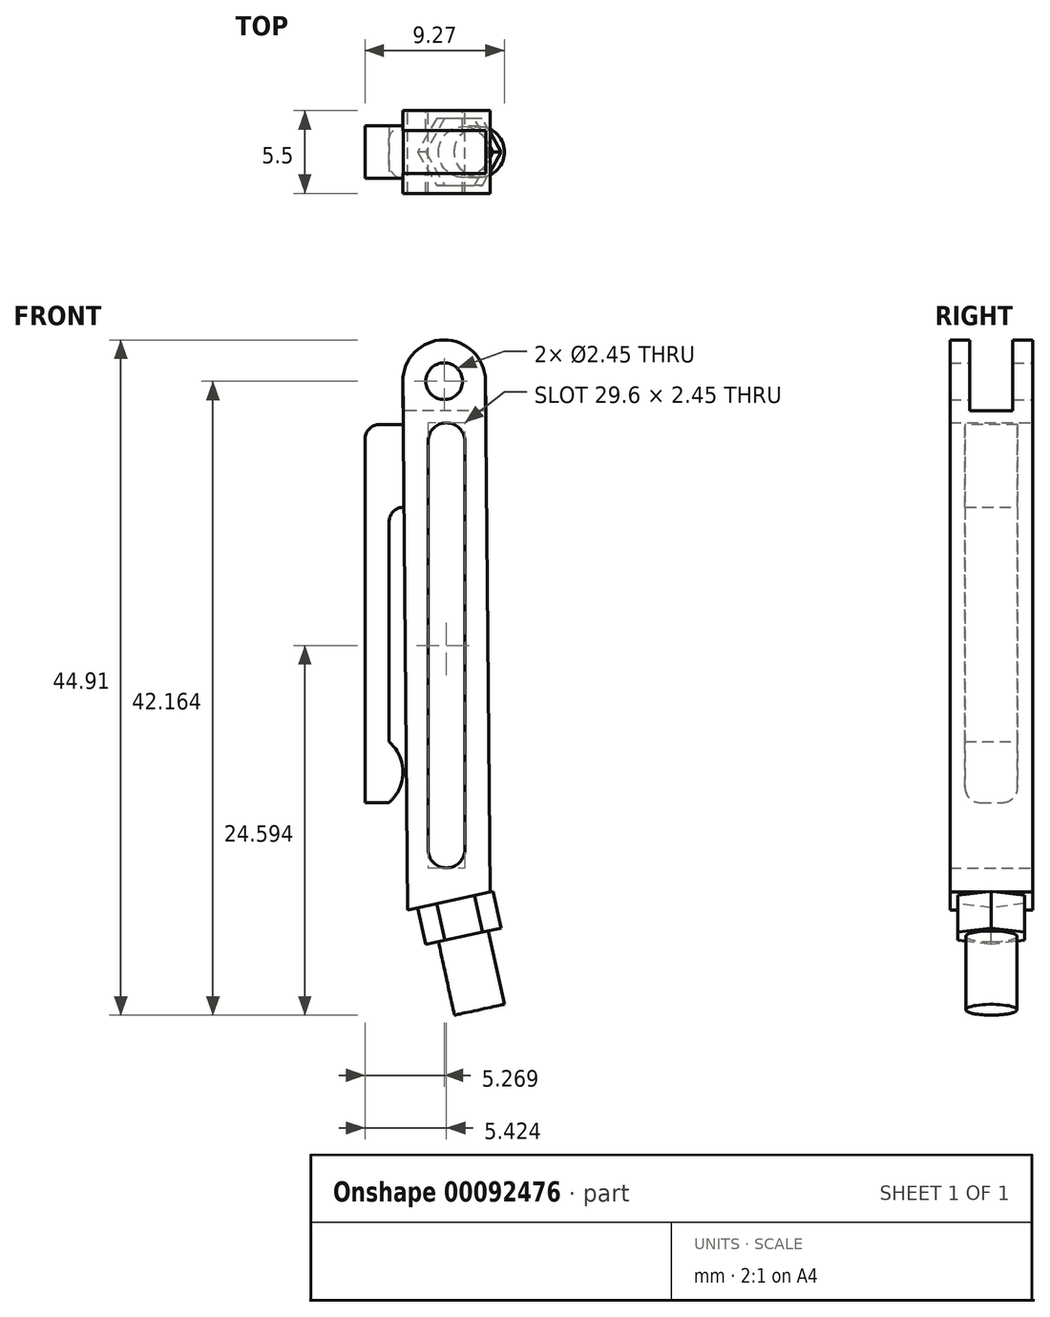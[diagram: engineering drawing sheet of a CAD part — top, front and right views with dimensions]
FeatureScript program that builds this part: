
annotation { "Feature Type Name" : "Feature", "Feature Type Description" : "" }
export const myFeature = defineFeature(function(context is Context, id is Id, definition is map)
    precondition{}
    {
        {
            var Q0;
            Q0=qCreatedBy(makeId("Front.planeOp"),FACE);
            var sketch = newSketch(context, id + "F0", { "sketchPlane" : qUnion([Q0])});
            skLineSegment(sketch, "E0.left", {"start": v(2.74, 2.18) * mm, "end": v(2.44, 36.18) * mm});
            skLineSegment(sketch, "E0.right", {"start": v(-2.75, 0.99) * mm, "end": v(-3.06, 36.13) * mm});
            skPoint(sketch, "E0.middle", {"position": v(-0.16, 18.58) * mm});
            skArc(sketch, "E1", {"start": v(2.44, 36.18) * mm, "mid": v(-0.34, 38.9) * mm, "end": v(-3.06, 36.13) * mm});
            skCircle(sketch, "E2", {"center": v(-0.31, 36.15) * mm, "radius": 1.23 * mm});
            skLineSegment(sketch, "E3.left", {"start": v(-1.38, 32.16) * mm, "end": v(-1.38, 5) * mm});
            skLineSegment(sketch, "E3.right", {"start": v(1.07, 32.16) * mm, "end": v(1.07, 5) * mm});
            skArc(sketch, "E4", {"start": v(1.07, 32.16) * mm, "mid": v(-0.16, 33.38) * mm, "end": v(-1.38, 32.16) * mm});
            skArc(sketch, "E5", {"start": v(-1.38, 5) * mm, "mid": v(-0.16, 3.78) * mm, "end": v(1.07, 5) * mm});
            skLineSegment(sketch, "E6", {"start": v(-2.75, 0.99) * mm, "end": v(2.74, 2.18) * mm});
            skSolve(sketch);
        }
        {
            var Q0;
            Q0=qSketchRegion(id+"F0",true);
            extrude(context, id + "F1", {"entities" : qUnion([Q0]), "depth" : 5.5 * mm, "symmetric" : true});
        }
        {
            var Q0;
            Q0=qCreatedBy(makeId("Front.planeOp"),FACE);
            var sketch = newSketch(context, id + "F2", { "sketchPlane" : qUnion([Q0])});
            skLineSegment(sketch, "E7", {"start": v(-2.9, 33.29) * mm, "end": v(-5.58, 33.29) * mm});
            skLineSegment(sketch, "E8", {"start": v(-5.58, 33.29) * mm, "end": v(-5.58, 8.14) * mm});
            skLineSegment(sketch, "E9", {"start": v(-5.58, 8.14) * mm, "end": v(-3.98, 8.14) * mm});
            skLineSegment(sketch, "E10", {"start": v(-3.98, 8.14) * mm, "end": v(-3.98, 27.78) * mm});
            skLineSegment(sketch, "E11", {"start": v(-3.98, 27.78) * mm, "end": v(-2.9, 27.78) * mm});
            skLineSegment(sketch, "E12", {"start": v(-2.9, 27.78) * mm, "end": v(-2.9, 33.29) * mm});
            skArc(sketch, "E13", {"start": v(-3.98, 8.14) * mm, "mid": v(-3.05, 10.16) * mm, "end": v(-3.98, 12.19) * mm});
            skSolve(sketch);
        }
        {
            var Q0;
            Q0=makeQuery(id+"F2.imprint","IMPRINT",FACE,{"disambiguationData":[TD([[makeQuery(id+"F2.imprint","IMPRINT",EDGE,{"derivedFrom":sQuery(id+"F2.wireOp",EDGE,"E7")}),1.0]])]});
            var Q1;
            {var subQ0=sQuery(id+"F2.wireOp",EDGE,"E13");Q1=makeQuery(id+"F2.imprint","IMPRINT",FACE,{"disambiguationData":[TD([[makeQuery(id+"F2.imprint","IMPRINT",EDGE,{"derivedFrom":subQ0}),1.0]])]});}
            extrude(context, id + "F3", {"entities" : qUnion([Q0, Q1]), "operationType" : NewBodyOperationType.ADD, "depth" : 3.5 * mm, "symmetric" : true});
        }
        {
            var Q0;
            Q0=qCreatedBy(makeId("Right.planeOp"),FACE);
            var sketch = newSketch(context, id + "F4", { "sketchPlane" : qUnion([Q0])});
            skLineSegment(sketch, "E14.bottom", {"start": v(1.44, 34.2) * mm, "end": v(-1.44, 34.2) * mm});
            skLineSegment(sketch, "E14.top", {"start": v(1.44, 40.18) * mm, "end": v(-1.44, 40.18) * mm});
            skLineSegment(sketch, "E14.left", {"start": v(1.44, 34.2) * mm, "end": v(1.44, 40.18) * mm});
            skLineSegment(sketch, "E14.right", {"start": v(-1.44, 34.2) * mm, "end": v(-1.44, 40.18) * mm});
            skPoint(sketch, "E14.middle", {"position": v(0, 37.2) * mm});
            skSolve(sketch);
        }
        {
            var Q0;
            Q0=qSketchRegion(id+"F4",true);
            extrude(context, id + "F5", {"entities" : qUnion([Q0]), "operationType" : NewBodyOperationType.REMOVE, "depth" : 26 * mm, "symmetric" : true});
        }
        {
            var Q0;
            Q0=makeQuery(id+"F3.opExtrude","SWEPT_EDGE",EDGE,{"disambiguationData":[OSD([sQuery(id+"F2.wireOp",EDGE,"E10"),sQuery(id+"F2.wireOp",EDGE,"E11")])]});
            fillet(context, id + "F6", {"entities" : qUnion([Q0]), "radius" : 1 * mm, "tangentPropagation" : true, "allowEdgeOverflow" : false});
        }
        {
            var Q0;
            Q0=makeQuery(id+"F3.opExtrude","SWEPT_EDGE",EDGE,{"disambiguationData":[OSD([sQuery(id+"F2.wireOp",EDGE,"E7"),sQuery(id+"F2.wireOp",EDGE,"E8")])]});
            var Q1;
            Q1=makeQuery(id+"F3.opExtrude","CAP_EDGE",EDGE,{"disambiguationData":[OSD([sQuery(id+"F2.wireOp",EDGE,"E9")])],"isStart":true});
            var Q2;
            Q2=makeQuery(id+"F3.opExtrude","CAP_EDGE",EDGE,{"disambiguationData":[OSD([sQuery(id+"F2.wireOp",EDGE,"E9")])],"isStart":false});
            fillet(context, id + "F7", {"entities" : qUnion([Q0, Q1, Q2]), "radius" : 1 * mm, "tangentPropagation" : true, "allowEdgeOverflow" : false});
        }
        {
            var Q0;
            Q0=makeQuery(id+"F1.opExtrude","SWEPT_FACE",FACE,{"disambiguationData":[OSD([sQuery(id+"F0.wireOp",EDGE,"E6")])]});
            cPlane(context, id + "F8", {"entities" : qUnion([Q0]), "cplaneType" : CPlaneType.OFFSET, "offset" : 0 * mm, "width" : 150 * mm, "height" : 150 * mm});
        }
        {
            var Q0;
            Q0=qCreatedBy(id+"F8.planeOp",FACE);
            var sketch = newSketch(context, id + "F9", { "sketchPlane" : qUnion([Q0])});
            skCircle(sketch, "E15.cCircle", {"center": v(0.79, 0) * mm, "radius": 2.23 * mm, "construction": true});
            skLineSegment(sketch, "E15.0", {"start": v(3.36, 0) * mm, "end": v(2.07, -2.23) * mm});
            skLineSegment(sketch, "E15.1", {"start": v(2.07, -2.23) * mm, "end": v(-0.5, -2.22) * mm});
            skLineSegment(sketch, "E15.2", {"start": v(-0.5, -2.22) * mm, "end": v(-1.78, 0) * mm});
            skLineSegment(sketch, "E15.3", {"start": v(-1.78, 0) * mm, "end": v(-0.5, 2.23) * mm});
            skLineSegment(sketch, "E15.4", {"start": v(-0.5, 2.23) * mm, "end": v(2.08, 2.22) * mm});
            skLineSegment(sketch, "E15.5", {"start": v(2.08, 2.22) * mm, "end": v(3.36, 0) * mm});
            skPoint(sketch, "E15.0.midPoint", {"position": v(2.71, -1.12) * mm});
            skCircle(sketch, "E16", {"center": v(0.79, 0) * mm, "radius": 1.7 * mm});
            skSolve(sketch);
        }
        {
            var Q0;
            Q0 = qSketchRegion(id + "F9", true);
            extrude(context, id + "F10", {"entities" : qUnion([Q0]), "operationType" : NewBodyOperationType.ADD, "depth" : 2.5 * mm});
        }
        {
            var Q0;
            Q0=makeQuery(id+"F10.boolean.opBoolean","SPLIT",FACE,{"disambiguationData":[TD([makeQuery(id+"F10.opExtrude","SWEPT_FACE",FACE,{"disambiguationData":[OSD([sQuery(id+"F9.wireOp",EDGE,"E16")])]})])],"derivedFrom":makeQuery(id+"F1.opExtrude","SWEPT_FACE",FACE,{"disambiguationData":[OSD([sQuery(id+"F0.wireOp",EDGE,"E6")])]})});
            extrude(context, id + "F11", {"entities" : qUnion([Q0]), "operationType" : NewBodyOperationType.ADD, "depth" : 7.5 * mm});
        }
    });
